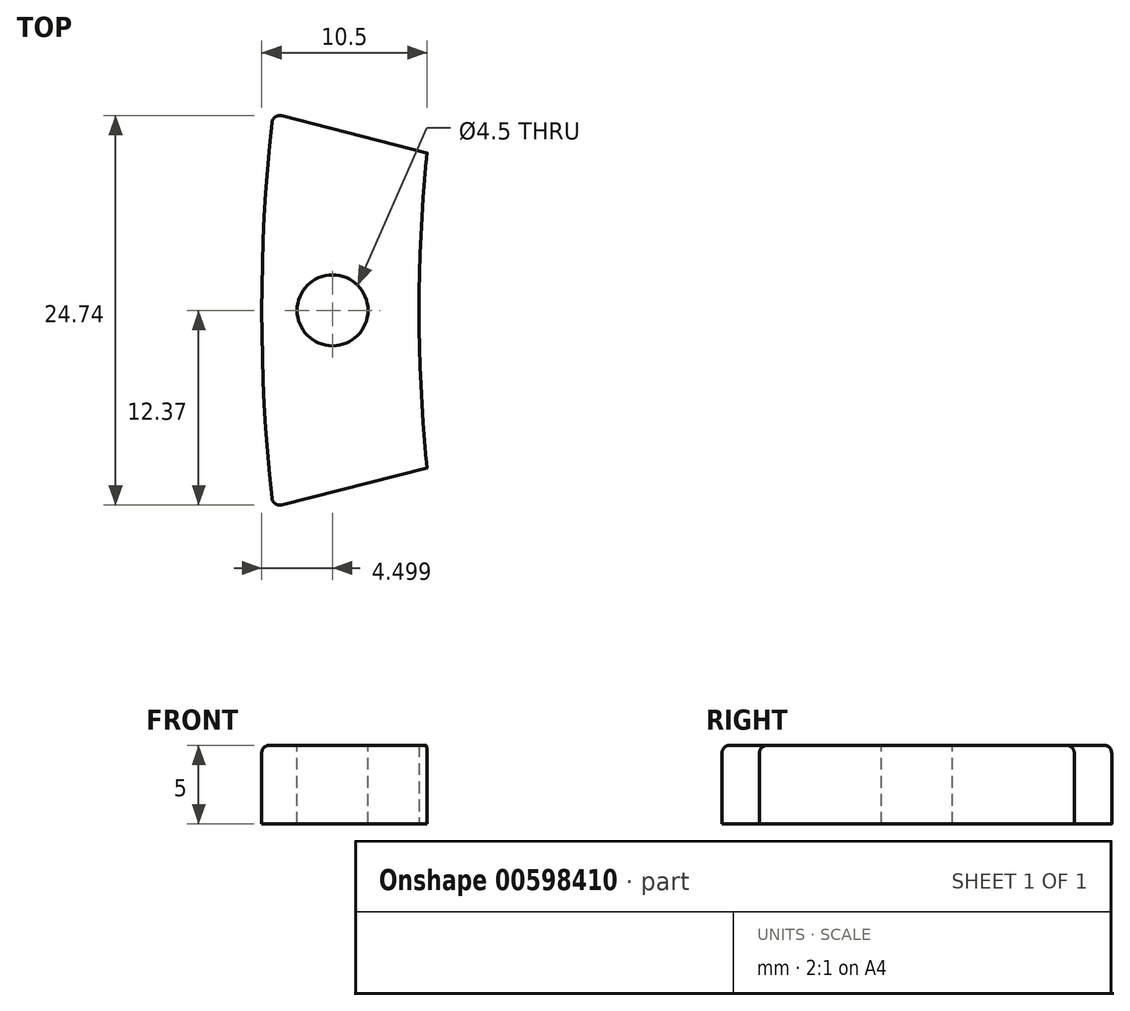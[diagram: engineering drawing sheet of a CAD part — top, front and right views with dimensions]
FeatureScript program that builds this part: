
annotation { "Feature Type Name" : "Feature", "Feature Type Description" : "" }
export const myFeature = defineFeature(function(context is Context, id is Id, definition is map)
    precondition{}
    {
        {
            var Q0;
            Q0=qCreatedBy(makeId("Top.planeOp"),FACE);
            var sketch = newSketch(context, id + "F0", { "sketchPlane" : qUnion([Q0])});
            skLineSegment(sketch, "E0", {"start": v(-9.79, -2.5) * mm, "end": v(0, 0) * mm});
            skLineSegment(sketch, "E1", {"start": v(-9.79, 22.5) * mm, "end": v(0, 20) * mm});
            skArc(sketch, "E2", {"start": v(0, 20) * mm, "mid": v(-0.5, 10) * mm, "end": v(0, 0) * mm});
            skArc(sketch, "E3", {"start": v(-9.79, 22.5) * mm, "mid": v(-10.5, 10) * mm, "end": v(-9.79, -2.5) * mm});
            skSolve(sketch);
        }
        {
            var Q0;
            Q0 = qSketchRegion(id + "F0", true);
            extrude(context, id + "F1", {"entities" : qUnion([Q0]), "depth" : 5 * mm, "offsetDistance" : 25 * mm});
        }
        {
            var Q0;
            Q0=makeQuery(id+"F1.opExtrude","CAP_FACE",FACE,{"disambiguationData":[OSD([sQuery(id+"F0.wireOp",EDGE,"E0"),sQuery(id+"F0.wireOp",EDGE,"E1"),sQuery(id+"F0.wireOp",EDGE,"E2"),sQuery(id+"F0.wireOp",EDGE,"E3")])],"isStart":false});
            var sketch = newSketch(context, id + "F2", { "sketchPlane" : qUnion([Q0])});
            skLineSegment(sketch, "E4", {"start": v(-0.5, 10) * mm, "end": v(-10.5, 10) * mm, "construction": true});
            skCircle(sketch, "E5", {"center": v(-6, 10) * mm, "radius": 2.25 * mm});
            skSolve(sketch);
        }
        {
            var Q0;
            Q0 = qSketchRegion(id + "F2", true);
            extrude(context, id + "F3", {"entities" : qUnion([Q0]), "operationType" : NewBodyOperationType.REMOVE, "oppositeDirection" : true, "depth" : 25 * mm, "offsetDistance" : 25 * mm});
        }
        {
            var Q0;
            Q0=makeQuery(id+"F1.opExtrude","CAP_EDGE",EDGE,{"disambiguationData":[OSD([sQuery(id+"F0.wireOp",EDGE,"E0")])],"isStart":false});
            var Q1;
            Q1=makeQuery(id+"F1.opExtrude","SWEPT_EDGE",EDGE,{"disambiguationData":[OSD([sQuery(id+"F0.wireOp",EDGE,"E0"),sQuery(id+"F0.wireOp",EDGE,"E3")])]});
            var Q2;
            Q2=makeQuery(id+"F1.opExtrude","CAP_EDGE",EDGE,{"disambiguationData":[OSD([sQuery(id+"F0.wireOp",EDGE,"E3")])],"isStart":false});
            var Q3;
            Q3=makeQuery(id+"F1.opExtrude","SWEPT_EDGE",EDGE,{"disambiguationData":[OSD([sQuery(id+"F0.wireOp",EDGE,"E1"),sQuery(id+"F0.wireOp",EDGE,"E3")])]});
            var Q4;
            Q4=makeQuery(id+"F1.opExtrude","CAP_EDGE",EDGE,{"disambiguationData":[OSD([sQuery(id+"F0.wireOp",EDGE,"E1")])],"isStart":false});
            fillet(context, id + "F4", {"entities" : qUnion([Q0, Q1, Q2, Q3, Q4]), "radius" : 0.5 * mm, "tangentPropagation" : true, "allowEdgeOverflow" : false});
        }
    });
